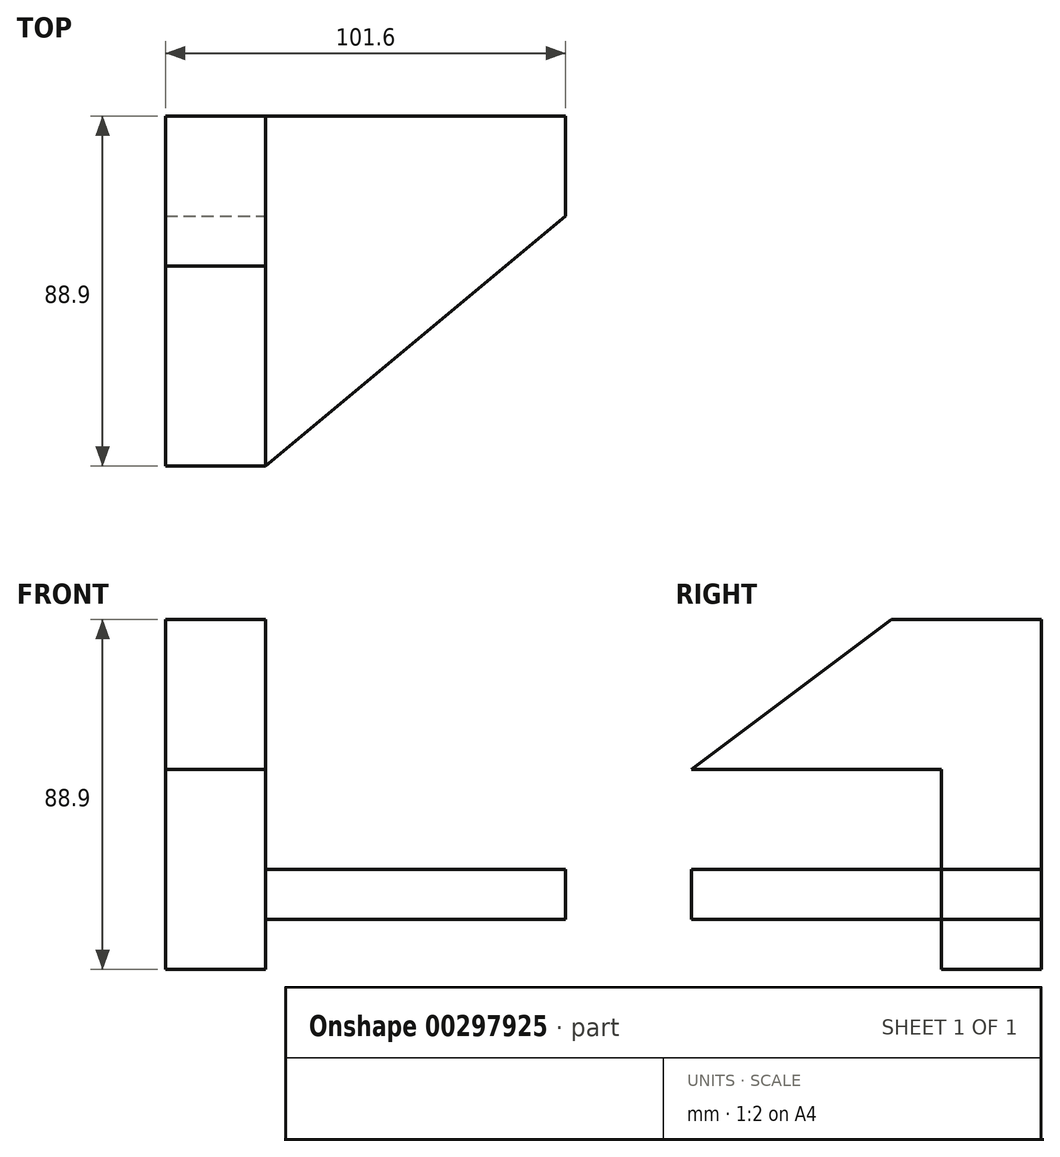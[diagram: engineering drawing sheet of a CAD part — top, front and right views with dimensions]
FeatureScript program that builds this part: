
annotation { "Feature Type Name" : "Feature", "Feature Type Description" : "" }
export const myFeature = defineFeature(function(context is Context, id is Id, definition is map)
    precondition{}
    {
        {
            var Q0;
            Q0=qCreatedBy(makeId("Front.planeOp"),FACE);
            var sketch = newSketch(context, id + "F0", { "sketchPlane" : qUnion([Q0])});
            skLineSegment(sketch, "E0.bottom", {"start": v(82.55, 50.8) * mm, "end": v(-82.55, 50.8) * mm});
            skLineSegment(sketch, "E0.top", {"start": v(82.55, -50.8) * mm, "end": v(-82.55, -50.8) * mm});
            skLineSegment(sketch, "E0.left", {"start": v(82.55, 50.8) * mm, "end": v(82.55, -50.8) * mm});
            skLineSegment(sketch, "E0.right", {"start": v(-82.55, 50.8) * mm, "end": v(-82.55, -50.8) * mm});
            skPoint(sketch, "E0.middle", {"position": v(0, 0) * mm});
            skLineSegment(sketch, "E1", {"start": v(-19.05, 50.8) * mm, "end": v(82.55, 0) * mm});
            skLineSegment(sketch, "E2.bottom", {"start": v(-82.55, -50.8) * mm, "end": v(-57.15, -50.8) * mm});
            skLineSegment(sketch, "E2.top", {"start": v(-82.55, 0) * mm, "end": v(-57.15, 0) * mm});
            skLineSegment(sketch, "E2.left", {"start": v(-82.55, -50.8) * mm, "end": v(-82.55, 0) * mm});
            skLineSegment(sketch, "E2.right", {"start": v(-57.15, -50.8) * mm, "end": v(-57.15, 0) * mm});
            skLineSegment(sketch, "E3.bottom", {"start": v(-57.15, -25.4) * mm, "end": v(19.05, -25.4) * mm});
            skLineSegment(sketch, "E3.top", {"start": v(-57.15, -38.1) * mm, "end": v(19.05, -38.1) * mm});
            skLineSegment(sketch, "E3.left", {"start": v(-57.15, -25.4) * mm, "end": v(-57.15, -38.1) * mm});
            skLineSegment(sketch, "E3.right", {"start": v(19.05, -25.4) * mm, "end": v(19.05, -38.1) * mm});
            skLineSegment(sketch, "E4.top", {"start": v(-82.55, 38.1) * mm, "end": v(-57.15, 38.1) * mm});
            skLineSegment(sketch, "E4.left", {"start": v(-82.55, 0) * mm, "end": v(-82.55, 38.1) * mm});
            skLineSegment(sketch, "E4.right", {"start": v(-57.15, 0) * mm, "end": v(-57.15, 38.1) * mm});
            skCircle(sketch, "E5", {"center": v(44.45, -12.7) * mm, "radius": 12.7 * mm});
            skSolve(sketch);
        }
        {
            var Q0;
            Q0=makeQuery(id+"F0.imprint","IMPRINT",FACE,{"disambiguationData":[TD([[makeQuery(id+"F0.imprint","IMPRINT",EDGE,{"derivedFrom":sQuery(id+"F0.wireOp",EDGE,"E3.bottom")}),-1.0]])]});
            var Q1;
            {var subQ1=sQuery(id+"F0.wireOp",EDGE,"E2.bottom");Q1=makeQuery(id+"F0.imprint","IMPRINT",FACE,{"disambiguationData":[TD([[makeQuery(id+"F0.imprint","IMPRINT",EDGE,{"derivedFrom":subQ1}),1.0]])]});}
            var Q2;
            Q2=makeQuery(id+"F0.imprint","IMPRINT",FACE,{"disambiguationData":[TD([[makeQuery(id+"F0.imprint","IMPRINT",EDGE,{"derivedFrom":sQuery(id+"F0.wireOp",EDGE,"E2.top")}),1.0]])]});
            extrude(context, id + "F1", {"entities" : qUnion([Q0, Q1, Q2]), "depth" : 88.9 * mm});
        }
        {
            var Q0;
            {var subQ1=sQuery(id+"F0.wireOp",EDGE,"E2.bottom");Q0=makeQuery(id+"F0.imprint","IMPRINT",FACE,{"disambiguationData":[TD([[makeQuery(id+"F0.imprint","IMPRINT",EDGE,{"derivedFrom":subQ1}),1.0]])]});}
            var Q1;
            {var subQ4=sQuery(id+"F0.wireOp",EDGE,"E0.top");Q1=makeQuery(id+"F0.imprint","IMPRINT",FACE,{"disambiguationData":[TD([[makeQuery(id+"F0.imprint","IMPRINT",EDGE,{"derivedFrom":subQ4}),-1.0]])]});}
            extrude(context, id + "F2", {"entities" : qUnion([Q0, Q1]), "operationType" : NewBodyOperationType.ADD, "depth" : 25.4 * mm});
        }
        {
            var Q0;
            Q0=makeQuery(id+"F1.opExtrude","SWEPT_FACE",FACE,{"disambiguationData":[OSD([sQuery(id+"F0.wireOp",EDGE,"E2.right"),sQuery(id+"F0.wireOp",EDGE,"E4.right")])]});
            var sketch = newSketch(context, id + "F3", { "sketchPlane" : qUnion([Q0])});
            skLineSegment(sketch, "E6", {"start": v(-38.1, 38.1) * mm, "end": v(-88.9, 0) * mm});
            skSolve(sketch);
        }
        {
            var Q0;
            Q0 = qSketchRegion(id + "F3", true);
            var Q1;
            {var subQ0=sQuery(id+"F3.wireOp",EDGE,"E6");Q1=makeQuery(id+"F3.imprint","IMPRINT",FACE,{"disambiguationData":[TD([[makeQuery(id+"F3.imprint","IMPRINT",EDGE,{"derivedFrom":subQ0}),-1.0]])]});}
            extrude(context, id + "F4", {"entities" : qUnion([Q0, Q1]), "operationType" : NewBodyOperationType.REMOVE, "oppositeDirection" : true, "depth" : 25.4 * mm});
        }
        {
            var Q0;
            Q0=makeQuery(id+"F1.opExtrude","SWEPT_FACE",FACE,{"disambiguationData":[OSD([sQuery(id+"F0.wireOp",EDGE,"E3.bottom")])]});
            var sketch = newSketch(context, id + "F5", { "sketchPlane" : qUnion([Q0])});
            skLineSegment(sketch, "E7", {"start": v(19.05, -25.4) * mm, "end": v(-57.15, -88.9) * mm});
            skSolve(sketch);
        }
        {
            var Q0;
            Q0 = qSketchRegion(id + "F5", true);
            var Q1;
            Q1=makeQuery(id+"F5.imprint","IMPRINT",FACE,{"disambiguationData":[TD([[makeQuery(id+"F5.imprint","IMPRINT",EDGE,{"derivedFrom":sQuery(id+"F5.wireOp",EDGE,"E7")}),1.0]])]});
            extrude(context, id + "F6", {"entities" : qUnion([Q0, Q1]), "operationType" : NewBodyOperationType.REMOVE, "oppositeDirection" : true, "depth" : 25.4 * mm});
        }
    });
